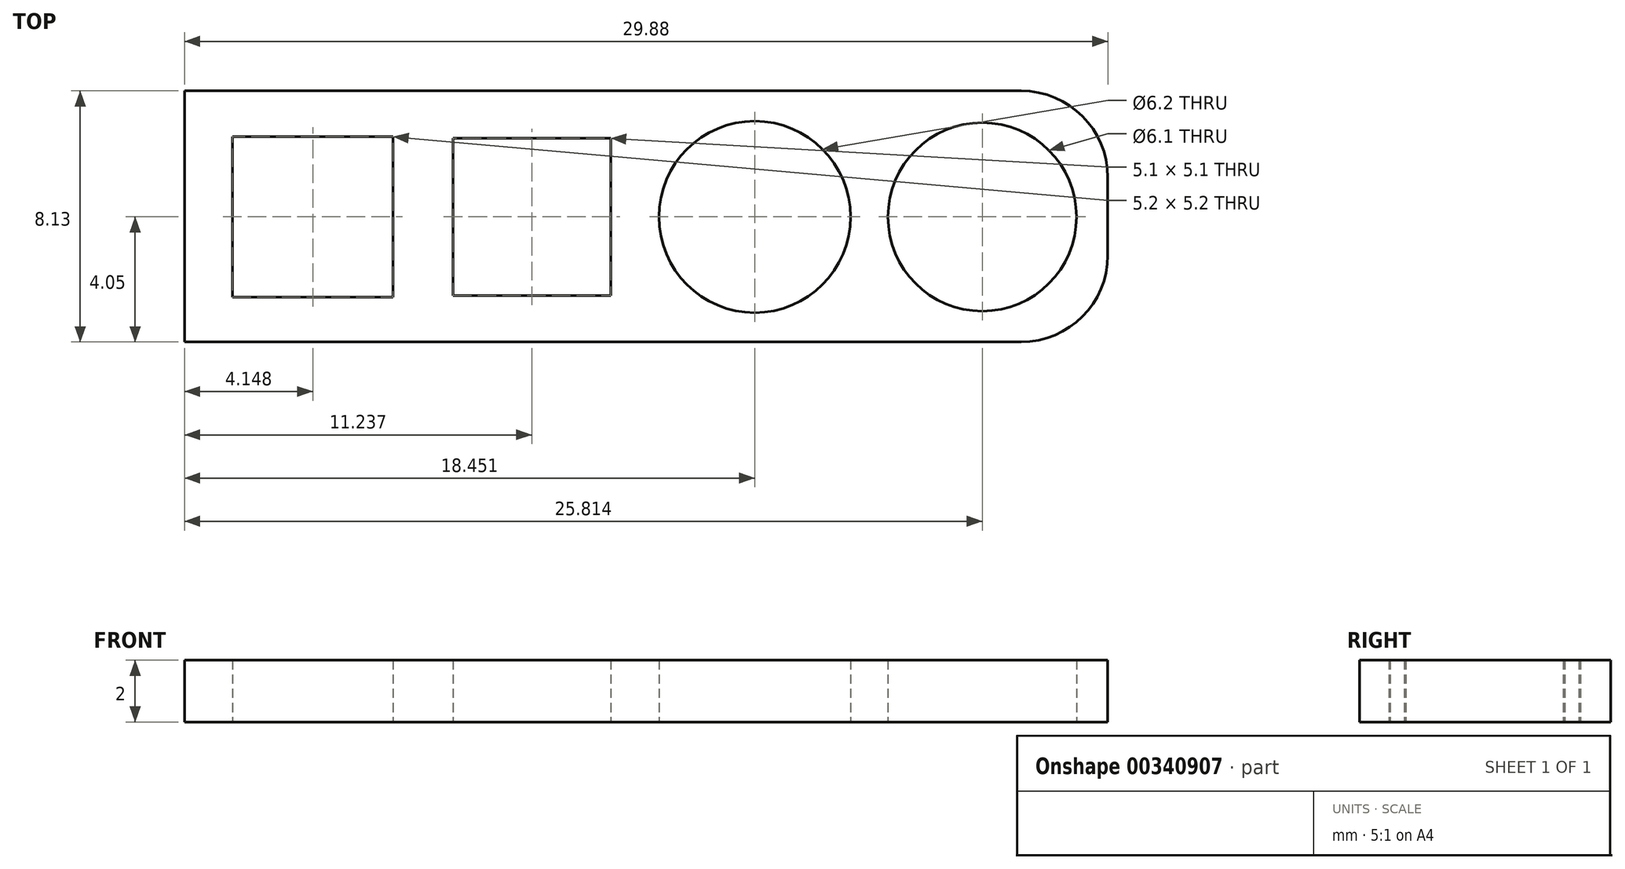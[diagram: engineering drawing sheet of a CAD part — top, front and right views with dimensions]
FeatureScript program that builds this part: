
annotation { "Feature Type Name" : "Feature", "Feature Type Description" : "" }
export const myFeature = defineFeature(function(context is Context, id is Id, definition is map)
    precondition{}
    {
        {
            var Q0;
            Q0=qCreatedBy(makeId("Top.planeOp"),FACE);
            var sketch = newSketch(context, id + "F0", { "sketchPlane" : qUnion([Q0])});
            skCircle(sketch, "E0", {"center": v(-18.94, 0) * mm, "radius": 3.05 * mm});
            skCircle(sketch, "E1", {"center": v(-26.3, 0) * mm, "radius": 3.1 * mm});
            skLineSegment(sketch, "E2.bottom", {"start": v(-30.96, -2.55) * mm, "end": v(-36.06, -2.55) * mm});
            skLineSegment(sketch, "E2.top", {"start": v(-30.96, 2.55) * mm, "end": v(-36.06, 2.55) * mm});
            skLineSegment(sketch, "E2.left", {"start": v(-30.96, -2.55) * mm, "end": v(-30.96, 2.55) * mm});
            skLineSegment(sketch, "E2.right", {"start": v(-36.06, -2.55) * mm, "end": v(-36.06, 2.55) * mm});
            skPoint(sketch, "E2.middle", {"position": v(-33.51, 0) * mm});
            skLineSegment(sketch, "E3.bottom", {"start": v(-43.2, -2.6) * mm, "end": v(-38, -2.6) * mm});
            skLineSegment(sketch, "E3.top", {"start": v(-43.2, 2.6) * mm, "end": v(-38, 2.6) * mm});
            skLineSegment(sketch, "E3.left", {"start": v(-43.2, -2.6) * mm, "end": v(-43.2, 2.6) * mm});
            skLineSegment(sketch, "E3.right", {"start": v(-38, -2.6) * mm, "end": v(-38, 2.6) * mm});
            skPoint(sketch, "E3.middle", {"position": v(-40.6, 0) * mm});
            skLineSegment(sketch, "E4.bottom", {"start": v(-44.75, 4.08) * mm, "end": v(-17.67, 4.08) * mm});
            skLineSegment(sketch, "E4.top", {"start": v(-44.75, -4.05) * mm, "end": v(-17.67, -4.05) * mm});
            skLineSegment(sketch, "E4.left", {"start": v(-44.75, 4.08) * mm, "end": v(-44.75, -4.05) * mm});
            skLineSegment(sketch, "E4.right", {"start": v(-14.87, 1.28) * mm, "end": v(-14.87, -1.25) * mm});
            skPoint(sketch, "E5.visualSharp", {"position": v(-14.87, 4.08) * mm});
            skArc(sketch, "E5.filletArc", {"start": v(-14.87, 1.28) * mm, "mid": v(-15.7, 3.26) * mm, "end": v(-17.67, 4.08) * mm});
            skPoint(sketch, "E6.visualSharp", {"position": v(-14.87, -4.05) * mm});
            skArc(sketch, "E6.filletArc", {"start": v(-17.67, -4.05) * mm, "mid": v(-15.7, -3.23) * mm, "end": v(-14.87, -1.25) * mm});
            skSolve(sketch);
        }
        {
            var Q0;
            Q0 = qSketchRegion(id + "F0", true);
            extrude(context, id + "F1", {"entities" : qUnion([Q0]), "depth" : 2 * mm, "offsetDistance" : 25 * mm});
        }
    });
